# Revit family: Geberit iCon klozet kapağı, ince tasarım_PRO_321691
name_source: partatom
category: Furniture
revit_build: Autodesk Revit 2018 (Build: 20190510_1515(x64)
units: mm (PartAtom-declared; Revit-internal decimal feet)

## family parameters
Always vertical = Yes
Cut with Voids When Loaded = No
OmniClass Number = 23.40.20.21
OmniClass Title = Toilet and Bath Specialties
Room Calculation Point = Yes
Shared = No
Work Plane-Based = No

## types (2) — shared parameters
Application range = Furniture
BIM Content Version = GEB MG 1.2
BIM Content revision date = 2020.05.18
Brand = Geberit
CW Connection = Yes
Characteristics = Zarif tasarım
Tam kapanan klozet kapağı
Antibakteriyel
Description = Geberit iCon klozet kapağı, ince tasarım
GEB_culture = tr-TR
GEB_generic_description = GBC
GEB_generic_manufacturer = generic
GEB_pimversion = 22.02.12
GEB_processing_type = T
GEB_reference = PRO_321691
GEB_translations = {"ATT_10673":"EAN code basic data","ATT_459792":"Renk / Yüzey","applicationPurposes":"Application purposes","application_range":"Application range","brandName":"Brand","characteristics":"Characteristics","content_creator":"BIM Content creator","content_date_changed":"BIM Content revision date","content_version":"BIM Content Version","key 1000":"Article number key","name":"Name","productBrand":"Product brand","scopeOfDelivery":"Scope of delivery","type":"Type","fixed_material":"Main material"}
HW Connection = No
IfcDescription = Geberit iCon klozet kapağı, ince tasarım
IfcExportAs = IfcFurniture
IfcExportType = WCSEAT
LOD300 = No
LOD400 = Yes
Main material = Geberit, Plastic, Opaque white
Manufacturer = Geberit
Name = Geberit iCon klozet kapağı, ince tasarım
Renk / Yüzey = Beyaz
Vent Connection = No
Waste Connection = Yes

## per-type parameters (varying)
| type | 500835_0_view | 574950000_0_view | Article number key | EAN code basic data |
| 574950000 Geberit iCon klozet kapağı, ince tasarım | No | Yes | 574950000 | 4022009343557 |
| 500.835.01.1 Geberit iCon klozet kapağı, ince tasarım | Yes | No | 500.835.01.1 | 4025410726018 |

## geometry (parser evidence)
native form markers: Blend x8, Sweep x20
no freeform markers — native parametric forms only
